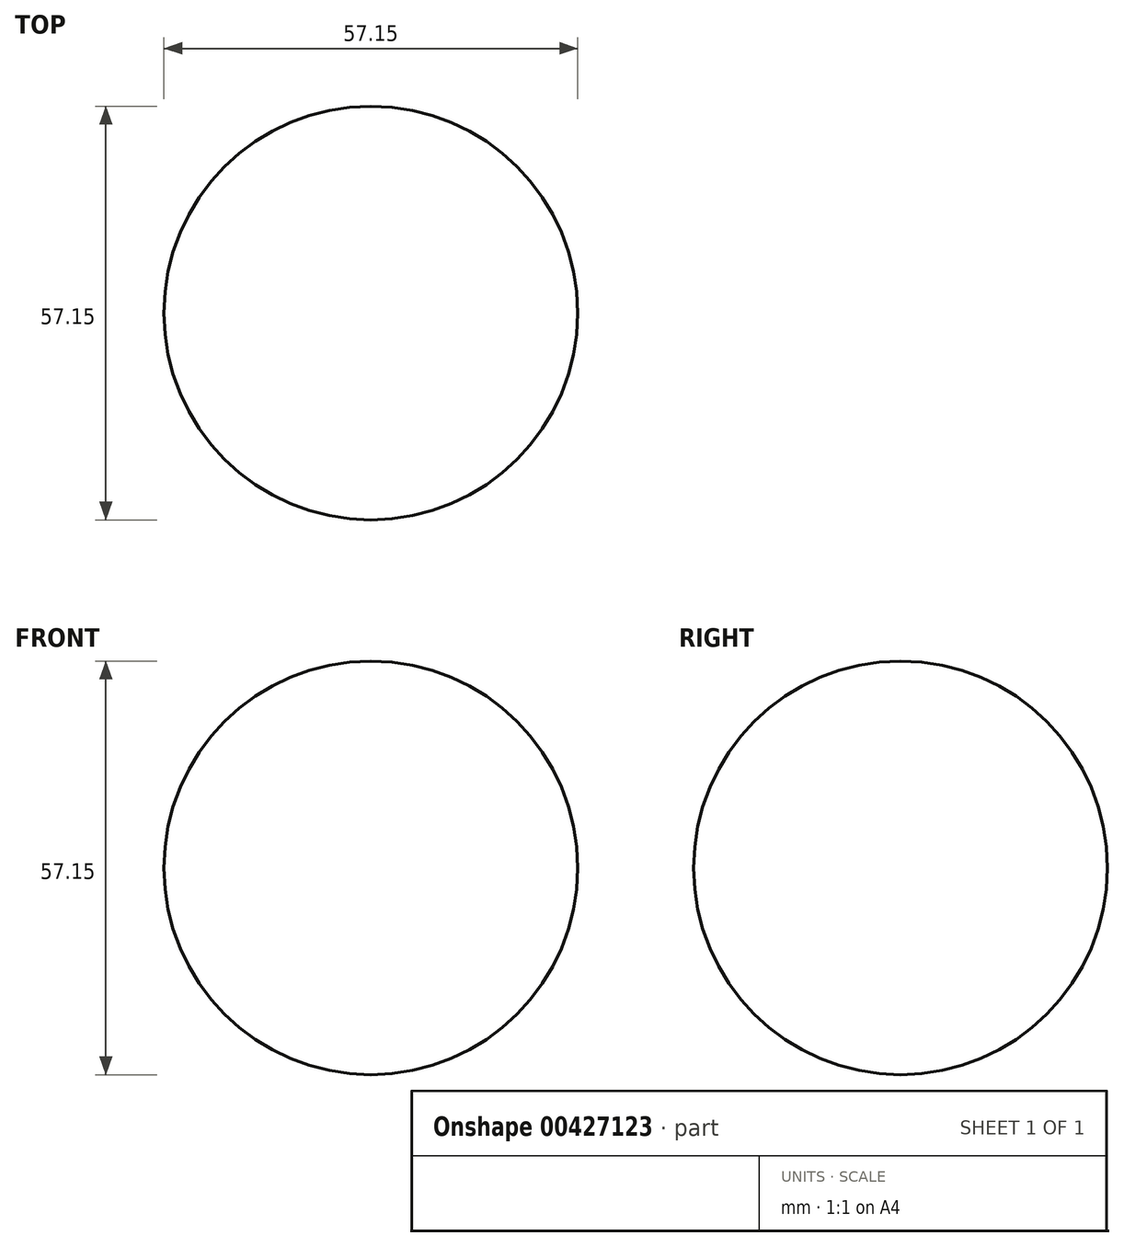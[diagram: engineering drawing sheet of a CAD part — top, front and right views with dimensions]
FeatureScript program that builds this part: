
annotation { "Feature Type Name" : "Feature", "Feature Type Description" : "" }
export const myFeature = defineFeature(function(context is Context, id is Id, definition is map)
    precondition{}
    {
        {
            var Q0;
            Q0=qCreatedBy(makeId("Front.planeOp"),FACE);
            var sketch = newSketch(context, id + "F0", { "sketchPlane" : qUnion([Q0])});
            skLineSegment(sketch, "E0", {"start": v(-70.84, 52.52) * mm, "end": v(58.03, 52.52) * mm});
            skSolve(sketch);
        }
        {
            var Q0;
            Q0=qCreatedBy(makeId("Front.planeOp"),FACE);
            var sketch = newSketch(context, id + "F1", { "sketchPlane" : qUnion([Q0])});
            skLineSegment(sketch, "E1", {"start": v(-39.05, 36.4) * mm, "end": v(-28.86, 36.4) * mm});
            skLineSegment(sketch, "E2", {"start": v(-28.86, 36.4) * mm, "end": v(35.35, 36.4) * mm});
            skLineSegment(sketch, "E3", {"start": v(35.35, 36.4) * mm, "end": v(35.35, -37.51) * mm});
            skLineSegment(sketch, "E4", {"start": v(35.35, -37.51) * mm, "end": v(-38.08, -37.51) * mm});
            skLineSegment(sketch, "E5", {"start": v(-38.08, -37.51) * mm, "end": v(-39.05, 36.4) * mm});
            skLineSegment(sketch, "E6", {"start": v(-26.75, 26.23) * mm, "end": v(-26.75, -30.92) * mm});
            skLineSegment(sketch, "E7", {"start": v(-26.75, -30.92) * mm, "end": v(30.4, -30.92) * mm});
            skLineSegment(sketch, "E8", {"start": v(30.4, -30.92) * mm, "end": v(30.4, 26.23) * mm});
            skLineSegment(sketch, "E9", {"start": v(30.4, 26.23) * mm, "end": v(-26.75, 26.23) * mm});
            skSolve(sketch);
        }
        {
            var Q0;
            Q0=makeQuery(id+"F1.imprint","IMPRINT",FACE,{"disambiguationData":[TD([[makeQuery(id+"F1.imprint","IMPRINT",EDGE,{"derivedFrom":sQuery(id+"F1.wireOp",EDGE,"E6")}),1.0]])]});
            extrude(context, id + "F2", {"entities" : qUnion([Q0]), "depth" : 57.15 * mm});
        }
        {
            var Q0;
            Q0=makeQuery(id+"F2.opExtrude","CAP_FACE",FACE,{"disambiguationData":[OSD([sQuery(id+"F1.wireOp",EDGE,"E6"),sQuery(id+"F1.wireOp",EDGE,"E7"),sQuery(id+"F1.wireOp",EDGE,"E8"),sQuery(id+"F1.wireOp",EDGE,"E9")])],"isStart":false});
            var Q1;
            Q1=makeQuery(id+"F2.opExtrude","CAP_FACE",FACE,{"disambiguationData":[OSD([sQuery(id+"F1.wireOp",EDGE,"E6"),sQuery(id+"F1.wireOp",EDGE,"E7"),sQuery(id+"F1.wireOp",EDGE,"E8"),sQuery(id+"F1.wireOp",EDGE,"E9")])],"isStart":true});
            var Q2;
            Q2=makeQuery(id+"F2.opExtrude","SWEPT_FACE",FACE,{"disambiguationData":[OSD([sQuery(id+"F1.wireOp",EDGE,"E7")])]});
            var Q3;
            Q3=makeQuery(id+"F2.opExtrude","SWEPT_FACE",FACE,{"disambiguationData":[OSD([sQuery(id+"F1.wireOp",EDGE,"E9")])]});
            fillet(context, id + "F3", {"entities" : qUnion([Q0, Q1, Q2, Q3]), "radius" : 28.57 * mm, "tangentPropagation" : true, "allowEdgeOverflow" : false});
        }
    });
